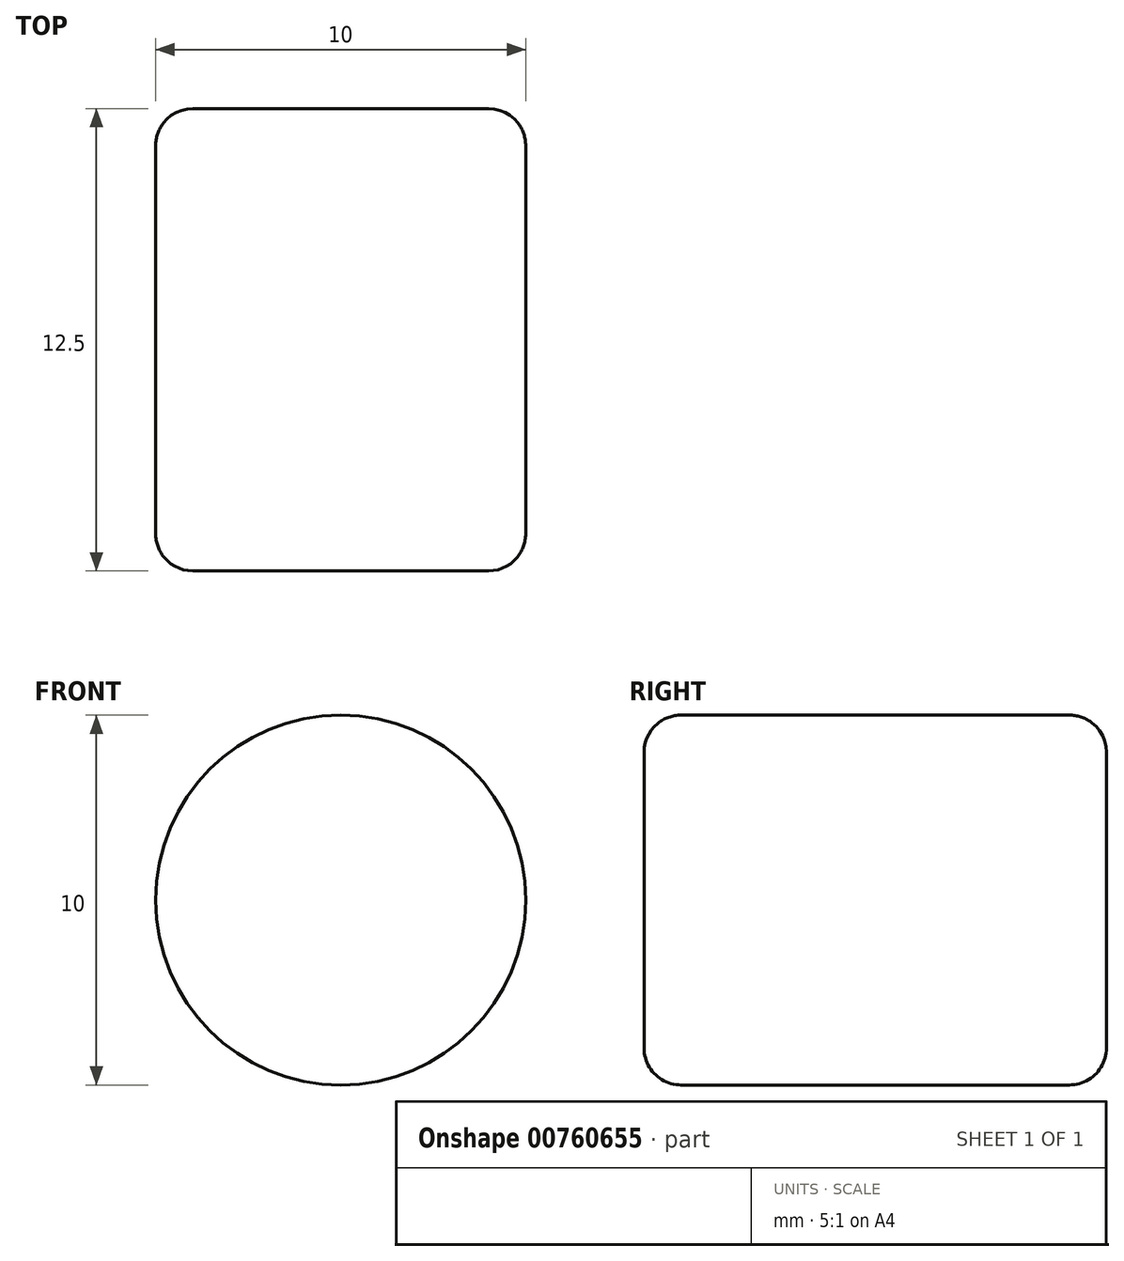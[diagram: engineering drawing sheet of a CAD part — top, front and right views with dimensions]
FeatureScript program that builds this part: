
annotation { "Feature Type Name" : "Feature", "Feature Type Description" : "" }
export const myFeature = defineFeature(function(context is Context, id is Id, definition is map)
    precondition{}
    {
        {
            var Q0;
            Q0=qCreatedBy(makeId("Front.planeOp"),FACE);
            var sketch = newSketch(context, id + "F0", { "sketchPlane" : qUnion([Q0])});
            skCircle(sketch, "E0", {"center": v(0, 0) * mm, "radius": 5 * mm});
            skSolve(sketch);
        }
        {
            var Q0;
            Q0=makeQuery(id+"F0.imprint","IMPRINT",FACE,{"disambiguationData":[TD([[makeQuery(id+"F0.imprint","IMPRINT",EDGE,{"derivedFrom":sQuery(id+"F0.wireOp",EDGE,"E0")}),1.0]])]});
            extrude(context, id + "F1", {"entities" : qUnion([Q0]), "depth" : 12.5 * mm, "offsetDistance" : 25 * mm});
        }
        {
            var Q0;
            Q0=makeQuery(id+"F1.opExtrude","CAP_FACE",FACE,{"disambiguationData":[OSD([sQuery(id+"F0.wireOp",EDGE,"E0")])],"isStart":false});
            var Q1;
            Q1=makeQuery(id+"F1.opExtrude","CAP_FACE",FACE,{"disambiguationData":[OSD([sQuery(id+"F0.wireOp",EDGE,"E0")])],"isStart":true});
            fillet(context, id + "F2", {"entities" : qUnion([Q0, Q1]), "radius" : 1 * mm, "tangentPropagation" : true, "allowEdgeOverflow" : false});
        }
    });
